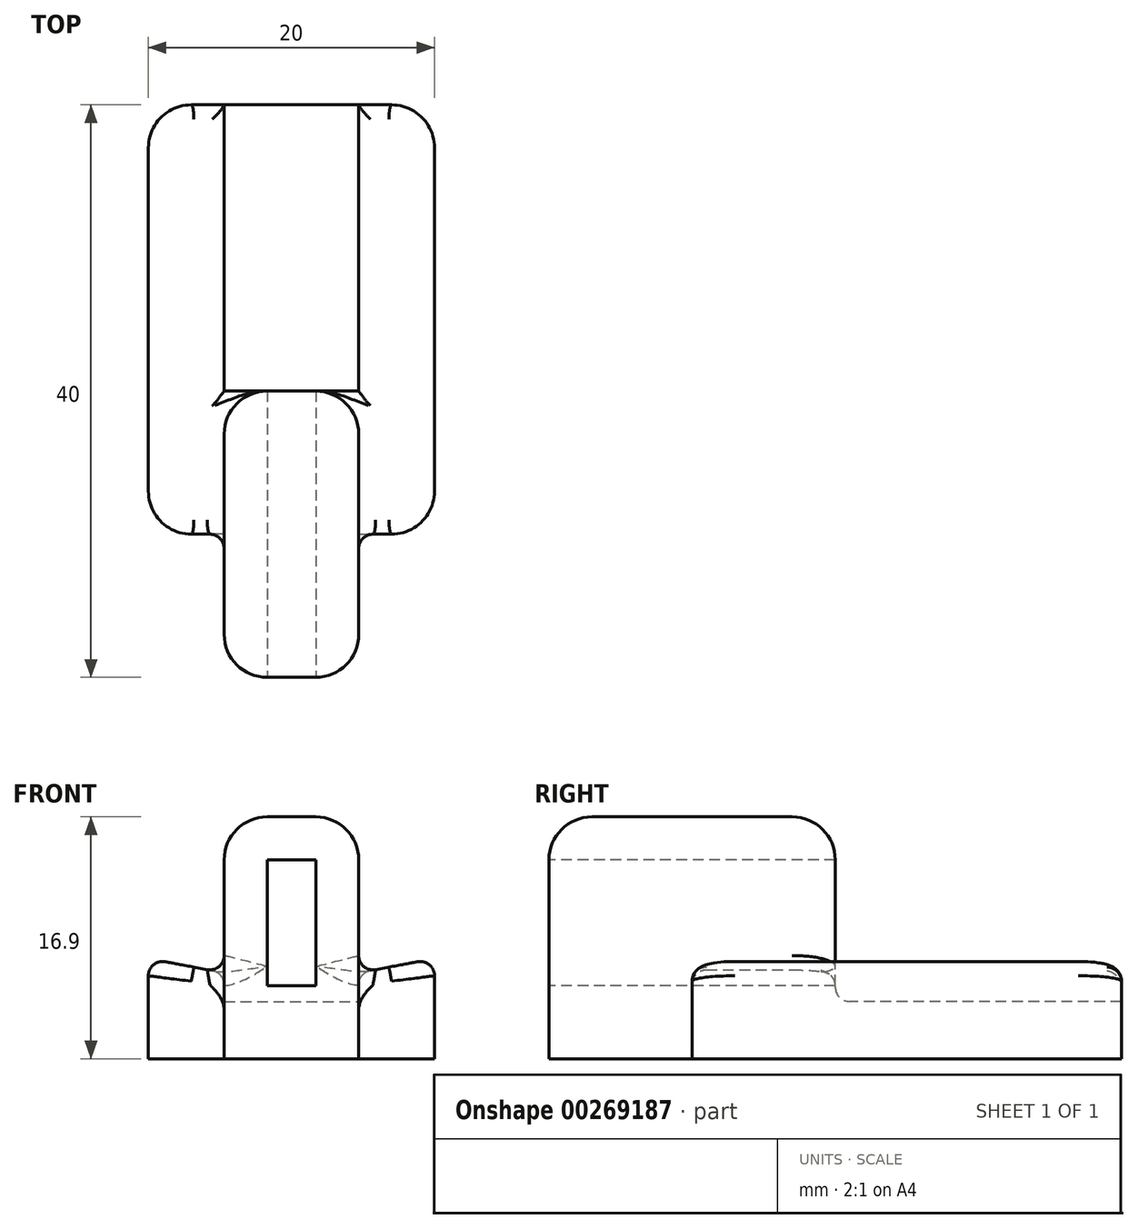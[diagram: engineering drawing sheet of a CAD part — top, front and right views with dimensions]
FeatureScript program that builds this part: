
annotation { "Feature Type Name" : "Feature", "Feature Type Description" : "" }
export const myFeature = defineFeature(function(context is Context, id is Id, definition is map)
    precondition{}
    {
        {
            assignVariable(context, id + "F0", {"name" : "BracketHeight", "anyValue" : 8.8});
        }
        {
            var Q0;
            Q0=qCreatedBy(makeId("Top.planeOp"),FACE);
            var sketch = newSketch(context, id + "F1", { "sketchPlane" : qUnion([Q0])});
            skLineSegment(sketch, "E0.bottom", {"start": v(4.7, -10) * mm, "end": v(-4.7, -10) * mm});
            skLineSegment(sketch, "E0.top", {"start": v(4.7, 10) * mm, "end": v(-4.7, 10) * mm});
            skLineSegment(sketch, "E0.left", {"start": v(4.7, -10) * mm, "end": v(4.7, 10) * mm});
            skLineSegment(sketch, "E0.right", {"start": v(-4.7, -10) * mm, "end": v(-4.7, 10) * mm});
            skPoint(sketch, "E0.middle", {"position": v(0, 0) * mm});
            skLineSegment(sketch, "E1", {"start": v(0, 23.9) * mm, "end": v(0, -29.95) * mm, "construction": true});
            skPoint(sketch, "E1.endSnap0", {"position": v(0, 10) * mm});
            skSolve(sketch);
        }
        {
            var Q0;
            Q0 = qSketchRegion(id + "F1", true);
            extrude(context, id + "F2", {"entities" : qUnion([Q0]), "depth" : (getVariable(context, 'BracketHeight') + 6) * mm});
        }
        {
            var Q0;
            Q0=makeQuery(id+"F2.opExtrude","SWEPT_FACE",FACE,{"disambiguationData":[OSD([sQuery(id+"F1.wireOp",EDGE,"E0.bottom")])]});
            var sketch = newSketch(context, id + "F3", { "sketchPlane" : qUnion([Q0])});
            skLineSegment(sketch, "E2.bottom", {"start": v(1.7, 11.8) * mm, "end": v(-1.7, 11.8) * mm});
            skLineSegment(sketch, "E2.top", {"start": v(1.7, 3) * mm, "end": v(-1.7, 3) * mm});
            skLineSegment(sketch, "E2.left", {"start": v(1.7, 11.8) * mm, "end": v(1.7, 3) * mm});
            skLineSegment(sketch, "E2.right", {"start": v(-1.7, 11.8) * mm, "end": v(-1.7, 3) * mm});
            skPoint(sketch, "E2.middle", {"position": v(0, 7.4) * mm});
            skLineSegment(sketch, "E3", {"start": v(-4.7, 14.8) * mm, "end": v(4.7, 0) * mm, "construction": true});
            skSolve(sketch);
        }
        {
            var Q0;
            Q0 = qSketchRegion(id + "F3", true);
            extrude(context, id + "F4", {"entities" : qUnion([Q0]), "operationType" : NewBodyOperationType.REMOVE, "endBound" : BoundingType.THROUGH_ALL, "oppositeDirection" : true, "depth" : 25 * mm});
        }
        {
            var Q0;
            Q0=qCreatedBy(makeId("Right.planeOp"),FACE);
            var sketch = newSketch(context, id + "F5", { "sketchPlane" : qUnion([Q0])});
            skLineSegment(sketch, "E4.bottom", {"start": v(0, 12.9) * mm, "end": v(30, 12.9) * mm});
            skLineSegment(sketch, "E4.top", {"start": v(0, 16.9) * mm, "end": v(30, 16.9) * mm});
            skLineSegment(sketch, "E4.left", {"start": v(0, 12.9) * mm, "end": v(0, 16.9) * mm});
            skLineSegment(sketch, "E4.right", {"start": v(30, 12.9) * mm, "end": v(30, 16.9) * mm});
            skSolve(sketch);
        }
        {
            var Q0;
            Q0 = qSketchRegion(id + "F5", true);
            extrude(context, id + "F6", {"entities" : qUnion([Q0]), "operationType" : NewBodyOperationType.ADD, "endBound" : BoundingType.SYMMETRIC, "depth" : 20 * mm, "hasSecondDirection" : true, "secondDirectionOppositeDirection" : true, "secondDirectionDepth" : 25 * mm});
        }
        {
            var Q0;
            Q0=makeQuery(id+"F2.opExtrude","CAP_FACE",FACE,{"disambiguationData":[OSD([sQuery(id+"F1.wireOp",EDGE,"E0.bottom"),sQuery(id+"F1.wireOp",EDGE,"E0.top"),sQuery(id+"F1.wireOp",EDGE,"E0.left"),sQuery(id+"F1.wireOp",EDGE,"E0.right")])],"isStart":false});
            var sketch = newSketch(context, id + "F7", { "sketchPlane" : qUnion([Q0])});
            skLineSegment(sketch, "E5.bottom", {"start": v(-4.7, 0) * mm, "end": v(4.7, 0) * mm});
            skLineSegment(sketch, "E5.top", {"start": v(-4.7, -10) * mm, "end": v(4.7, -10) * mm});
            skLineSegment(sketch, "E5.left", {"start": v(-4.7, 0) * mm, "end": v(-4.7, -10) * mm});
            skLineSegment(sketch, "E5.right", {"start": v(4.7, 0) * mm, "end": v(4.7, -10) * mm});
            skSolve(sketch);
        }
        {
            var Q0;
            Q0 = qSketchRegion(id + "F7", true);
            var Q1;
            Q1=makeQuery(id+"F6.opExtrude","SWEPT_FACE",FACE,{"disambiguationData":[OSD([sQuery(id+"F5.wireOp",EDGE,"E4.top")])]});
            extrude(context, id + "F8", {"entities" : qUnion([Q0]), "operationType" : NewBodyOperationType.ADD, "endBound" : BoundingType.UP_TO_SURFACE, "endBoundEntityFace" : qUnion([Q1]), "depth" : 25 * mm});
        }
        {
            var Q0;
            {var subQ1=sQuery(id+"F5.wireOp",EDGE,"E4.left");Q0=makeQuery(id+"F8.boolean.opBoolean","SPLIT",FACE,{"disambiguationData":[TD([makeQuery(id+"F2.opExtrude","SWEPT_FACE",FACE,{"disambiguationData":[OSD([sQuery(id+"F1.wireOp",EDGE,"E0.right")])]})])],"derivedFrom":makeQuery(id+"F6.opExtrude","SWEPT_FACE",FACE,{"disambiguationData":[OSD([subQ1])]})});}
            var sketch = newSketch(context, id + "F9", { "sketchPlane" : qUnion([Q0])});
            skLineSegment(sketch, "E6", {"start": v(-10, 12.9) * mm, "end": v(-10, 9.9) * mm});
            skLineSegment(sketch, "E7", {"start": v(-10, 9.9) * mm, "end": v(-4.7, 10.9) * mm});
            skLineSegment(sketch, "E8", {"start": v(-4.7, 10.9) * mm, "end": v(-4.7, 12.9) * mm});
            skLineSegment(sketch, "E9", {"start": v(-4.7, 12.9) * mm, "end": v(-10, 12.9) * mm});
            skLineSegment(sketch, "E10.MirrorCS", {"start": v(10, 9.9) * mm, "end": v(4.7, 10.9) * mm});
            skLineSegment(sketch, "E11.MirrorCS", {"start": v(10, 12.9) * mm, "end": v(10, 9.9) * mm});
            skLineSegment(sketch, "E12.MirrorCS", {"start": v(4.7, 10.9) * mm, "end": v(4.7, 12.9) * mm});
            skLineSegment(sketch, "E13.MirrorCS", {"start": v(4.7, 12.9) * mm, "end": v(10, 12.9) * mm});
            skSolve(sketch);
        }
        {
            var Q0;
            Q0 = qSketchRegion(id + "F9", true);
            var Q1;
            Q1=makeQuery(id+"F6.opExtrude","SWEPT_FACE",FACE,{"disambiguationData":[OSD([sQuery(id+"F5.wireOp",EDGE,"E4.right")])]});
            extrude(context, id + "F10", {"entities" : qUnion([Q0]), "operationType" : NewBodyOperationType.ADD, "endBound" : BoundingType.UP_TO_SURFACE, "oppositeDirection" : true, "endBoundEntityFace" : qUnion([Q1]), "depth" : 25 * mm});
        }
        {
            var Q0;
            Q0=makeQuery(id+"F2.opExtrude","SWEPT_BODY",BODY,{"disambiguationData":[OSD([sQuery(id+"F1.wireOp",EDGE,"E0.bottom"),sQuery(id+"F1.wireOp",EDGE,"E0.top"),sQuery(id+"F1.wireOp",EDGE,"E0.left"),sQuery(id+"F1.wireOp",EDGE,"E0.right")])]});
            var Q1;
            Q1=sQuery(id+"F1.wireOp",EDGE,"E1");
            transform(context, id + "F11", {"entities" : qUnion([Q0]), "transformType" : TransformType.ROTATION, "transformAxis" : qUnion([Q1]), "angle" : 180 * degree, "makeCopy" : false});
        }
        {
            var Q0;
            Q0=makeQuery(id+"F2.opExtrude","CAP_FACE",FACE,{"disambiguationData":[OSD([sQuery(id+"F1.wireOp",EDGE,"E0.bottom"),sQuery(id+"F1.wireOp",EDGE,"E0.top"),sQuery(id+"F1.wireOp",EDGE,"E0.left"),sQuery(id+"F1.wireOp",EDGE,"E0.right")])],"isStart":true});
            var Q1;
            Q1=makeQuery(id+"F8.boolean.opBoolean","MERGE",EDGE,{"derivedFrom":[makeQuery(id+"F2.opExtrude","SWEPT_EDGE",EDGE,{"disambiguationData":[OSD([sQuery(id+"F1.wireOp",EDGE,"E0.bottom"),sQuery(id+"F1.wireOp",EDGE,"E0.left")])]}),makeQuery(id+"F8.opExtrude","SWEPT_EDGE",EDGE,{"disambiguationData":[OSD([sQuery(id+"F7.wireOp",EDGE,"E5.top"),sQuery(id+"F7.wireOp",EDGE,"E5.right")])]})]});
            var Q2;
            Q2=makeQuery(id+"F8.boolean.opBoolean","MERGE",EDGE,{"derivedFrom":[makeQuery(id+"F2.opExtrude","SWEPT_EDGE",EDGE,{"disambiguationData":[OSD([sQuery(id+"F1.wireOp",EDGE,"E0.bottom"),sQuery(id+"F1.wireOp",EDGE,"E0.right")])]}),makeQuery(id+"F8.opExtrude","SWEPT_EDGE",EDGE,{"disambiguationData":[OSD([sQuery(id+"F7.wireOp",EDGE,"E5.top"),sQuery(id+"F7.wireOp",EDGE,"E5.left")])]})]});
            var Q3;
            {var subQ0=sQuery(id+"F1.wireOp",EDGE,"E0.left");var subQ1=sQuery(id+"F1.wireOp",EDGE,"E0.top");Q3=makeQuery(id+"F10.boolean.opBoolean","SPLIT",EDGE,{"disambiguationData":[TD([makeQuery(id+"F2.opExtrude","CAP_FACE",FACE,{"disambiguationData":[OSD([sQuery(id+"F1.wireOp",EDGE,"E0.bottom"),subQ1,subQ0,sQuery(id+"F1.wireOp",EDGE,"E0.right")])],"isStart":true})])],"derivedFrom":makeQuery(id+"F2.opExtrude","SWEPT_EDGE",EDGE,{"disambiguationData":[OSD([subQ1,subQ0])]})});}
            var Q4;
            {var subQ0=sQuery(id+"F1.wireOp",EDGE,"E0.right");var subQ1=sQuery(id+"F1.wireOp",EDGE,"E0.top");Q4=makeQuery(id+"F10.boolean.opBoolean","SPLIT",EDGE,{"disambiguationData":[TD([makeQuery(id+"F2.opExtrude","CAP_FACE",FACE,{"disambiguationData":[OSD([sQuery(id+"F1.wireOp",EDGE,"E0.bottom"),subQ1,sQuery(id+"F1.wireOp",EDGE,"E0.left"),subQ0])],"isStart":true})])],"derivedFrom":makeQuery(id+"F2.opExtrude","SWEPT_EDGE",EDGE,{"disambiguationData":[OSD([subQ1,subQ0])]})});}
            var Q5;
            Q5=makeQuery(id+"F10.boolean.opBoolean","MERGE",EDGE,{"derivedFrom":[makeQuery(id+"F6.opExtrude","CAP_EDGE",EDGE,{"disambiguationData":[OSD([sQuery(id+"F5.wireOp",EDGE,"E4.left")])],"isStart":false}),makeQuery(id+"F10.opExtrude","CAP_EDGE",EDGE,{"disambiguationData":[OSD([sQuery(id+"F9.wireOp",EDGE,"E11.MirrorCS")])],"isStart":true})]});
            var Q6;
            Q6=makeQuery(id+"F10.boolean.opBoolean","MERGE",EDGE,{"derivedFrom":[makeQuery(id+"F6.opExtrude","CAP_EDGE",EDGE,{"disambiguationData":[OSD([sQuery(id+"F5.wireOp",EDGE,"E4.left")])],"isStart":true}),makeQuery(id+"F10.opExtrude","CAP_EDGE",EDGE,{"disambiguationData":[OSD([sQuery(id+"F9.wireOp",EDGE,"E6")])],"isStart":true})]});
            var Q7;
            {var subQ0=sQuery(id+"F5.wireOp",EDGE,"E4.right");Q7=makeQuery(id+"F10.boolean.opBoolean","MERGE",EDGE,{"derivedFrom":[makeQuery(id+"F6.opExtrude","CAP_EDGE",EDGE,{"disambiguationData":[OSD([subQ0])],"isStart":true}),makeQuery(id+"F10.opExtrude","TWEAK_EDGE",EDGE,{"derivedFrom":[makeQuery(id+"F6.opExtrude","SWEPT_FACE",FACE,{"disambiguationData":[OSD([subQ0])]}),makeQuery(id+"F9.imprint","IMPRINT",EDGE,{"derivedFrom":sQuery(id+"F9.wireOp",EDGE,"E6")})]})]});}
            var Q8;
            {var subQ0=sQuery(id+"F5.wireOp",EDGE,"E4.right");Q8=makeQuery(id+"F10.boolean.opBoolean","MERGE",EDGE,{"derivedFrom":[makeQuery(id+"F6.opExtrude","CAP_EDGE",EDGE,{"disambiguationData":[OSD([subQ0])],"isStart":false}),makeQuery(id+"F10.opExtrude","TWEAK_EDGE",EDGE,{"derivedFrom":[makeQuery(id+"F6.opExtrude","SWEPT_FACE",FACE,{"disambiguationData":[OSD([subQ0])]}),makeQuery(id+"F9.imprint","IMPRINT",EDGE,{"derivedFrom":sQuery(id+"F9.wireOp",EDGE,"E11.MirrorCS")})]})]});}
            fillet(context, id + "F12", {"entities" : qUnion([Q0, Q1, Q2, Q3, Q4, Q5, Q6, Q7, Q8]), "radius" : 3 * mm, "tangentPropagation" : true, "allowEdgeOverflow" : false});
        }
        {
            var Q0;
            {var subQ0=makeQuery(id+"F10.opExtrude","SWEPT_FACE",FACE,{"disambiguationData":[OSD([sQuery(id+"F9.wireOp",EDGE,"E10.MirrorCS")])]});var subQ1=sQuery(id+"F1.wireOp",EDGE,"E0.left");var subQ2=sQuery(id+"F1.wireOp",EDGE,"E0.top");Q0=makeQuery(id+"F12.opFillet","BLEND_EDGE",EDGE,{"blendedFrom":[makeQuery(id+"F10.boolean.opBoolean","SPLIT",EDGE,{"disambiguationData":[TD([makeQuery(id+"F2.opExtrude","CAP_FACE",FACE,{"disambiguationData":[OSD([sQuery(id+"F1.wireOp",EDGE,"E0.bottom"),subQ2,subQ1,sQuery(id+"F1.wireOp",EDGE,"E0.right")])],"isStart":true})])],"derivedFrom":makeQuery(id+"F2.opExtrude","SWEPT_EDGE",EDGE,{"disambiguationData":[OSD([subQ2,subQ1])]})}),subQ0],"blendedInto":[subQ0]});}
            var Q1;
            {var subQ0=makeQuery(id+"F10.opExtrude","SWEPT_FACE",FACE,{"disambiguationData":[OSD([sQuery(id+"F9.wireOp",EDGE,"E7")])]});var subQ1=sQuery(id+"F1.wireOp",EDGE,"E0.right");var subQ2=sQuery(id+"F1.wireOp",EDGE,"E0.top");Q1=makeQuery(id+"F12.opFillet","BLEND_EDGE",EDGE,{"blendedFrom":[makeQuery(id+"F10.boolean.opBoolean","SPLIT",EDGE,{"disambiguationData":[TD([makeQuery(id+"F2.opExtrude","CAP_FACE",FACE,{"disambiguationData":[OSD([sQuery(id+"F1.wireOp",EDGE,"E0.bottom"),subQ2,sQuery(id+"F1.wireOp",EDGE,"E0.left"),subQ1])],"isStart":true})])],"derivedFrom":makeQuery(id+"F2.opExtrude","SWEPT_EDGE",EDGE,{"disambiguationData":[OSD([subQ2,subQ1])]})}),subQ0],"blendedInto":[subQ0]});}
            var Q2;
            Q2=makeQuery(id+"F10.opExtrude","SWEPT_EDGE",EDGE,{"disambiguationData":[OSD([sQuery(id+"F9.wireOp",EDGE,"E12.MirrorCS"),sQuery(id+"F9.wireOp",EDGE,"E13.MirrorCS")])]});
            var Q3;
            Q3=makeQuery(id+"F10.opExtrude","SWEPT_EDGE",EDGE,{"disambiguationData":[OSD([sQuery(id+"F1.wireOp",EDGE,"E0.right"),sQuery(id+"F5.wireOp",EDGE,"E4.left"),sQuery(id+"F7.wireOp",EDGE,"E5.bottom"),sQuery(id+"F7.wireOp",EDGE,"E5.left"),sQuery(id+"F9.wireOp",EDGE,"E8"),sQuery(id+"F9.wireOp",EDGE,"E9")])]});
            var Q4;
            Q4=makeQuery(id+"F6.boolean.opBoolean","INTERSECT",EDGE,{"derivedFrom":[makeQuery(id+"F2.opExtrude","SWEPT_FACE",FACE,{"disambiguationData":[OSD([sQuery(id+"F1.wireOp",EDGE,"E0.top")])]}),makeQuery(id+"F6.opExtrude","SWEPT_FACE",FACE,{"disambiguationData":[OSD([sQuery(id+"F5.wireOp",EDGE,"E4.bottom")])]})]});
            var Q5;
            Q5=makeQuery(id+"F10.opExtrude","TWEAK_EDGE",EDGE,{"derivedFrom":[makeQuery(id+"F6.opExtrude","SWEPT_FACE",FACE,{"disambiguationData":[OSD([sQuery(id+"F5.wireOp",EDGE,"E4.right")])]}),makeQuery(id+"F9.imprint","IMPRINT",EDGE,{"derivedFrom":sQuery(id+"F9.wireOp",EDGE,"E12.MirrorCS")})]});
            var Q6;
            Q6=makeQuery(id+"F10.opExtrude","TWEAK_EDGE",EDGE,{"derivedFrom":[makeQuery(id+"F6.opExtrude","SWEPT_FACE",FACE,{"disambiguationData":[OSD([sQuery(id+"F5.wireOp",EDGE,"E4.right")])]}),makeQuery(id+"F9.imprint","IMPRINT",EDGE,{"derivedFrom":sQuery(id+"F9.wireOp",EDGE,"E10.MirrorCS")})]});
            var Q7;
            Q7=makeQuery(id+"F10.opExtrude","TWEAK_EDGE",EDGE,{"derivedFrom":[makeQuery(id+"F6.opExtrude","SWEPT_FACE",FACE,{"disambiguationData":[OSD([sQuery(id+"F5.wireOp",EDGE,"E4.right")])]}),makeQuery(id+"F9.imprint","IMPRINT",EDGE,{"derivedFrom":sQuery(id+"F9.wireOp",EDGE,"E7")})]});
            var Q8;
            Q8=makeQuery(id+"F10.opExtrude","SWEPT_EDGE",EDGE,{"disambiguationData":[OSD([sQuery(id+"F9.wireOp",EDGE,"E10.MirrorCS"),sQuery(id+"F9.wireOp",EDGE,"E11.MirrorCS")])]});
            var Q9;
            Q9=makeQuery(id+"F10.opExtrude","SWEPT_EDGE",EDGE,{"disambiguationData":[OSD([sQuery(id+"F9.wireOp",EDGE,"E6"),sQuery(id+"F9.wireOp",EDGE,"E7")])]});
            var Q10;
            Q10=makeQuery(id+"F10.opExtrude","CAP_EDGE",EDGE,{"disambiguationData":[OSD([sQuery(id+"F9.wireOp",EDGE,"E7")])],"isStart":true});
            var Q11;
            Q11=makeQuery(id+"F10.opExtrude","CAP_EDGE",EDGE,{"disambiguationData":[OSD([sQuery(id+"F9.wireOp",EDGE,"E10.MirrorCS")])],"isStart":true});
            var Q12;
            {var subQ0=sQuery(id+"F5.wireOp",EDGE,"E4.right");var subQ1=sQuery(id+"F9.wireOp",EDGE,"E8");var subQ2=sQuery(id+"F9.wireOp",EDGE,"E7");Q12=makeQuery(id+"F10.boolean.opBoolean","SPLIT",EDGE,{"disambiguationData":[TD([makeQuery(id+"F6.opExtrude","SWEPT_FACE",FACE,{"disambiguationData":[OSD([subQ0])]})])],"derivedFrom":makeQuery(id+"F10.opExtrude","SWEPT_EDGE",EDGE,{"disambiguationData":[OSD([subQ2,subQ1])]})});}
            var Q13;
            {var subQ0=sQuery(id+"F5.wireOp",EDGE,"E4.right");var subQ1=sQuery(id+"F9.wireOp",EDGE,"E12.MirrorCS");var subQ2=sQuery(id+"F9.wireOp",EDGE,"E10.MirrorCS");Q13=makeQuery(id+"F10.boolean.opBoolean","SPLIT",EDGE,{"disambiguationData":[TD([makeQuery(id+"F6.opExtrude","SWEPT_FACE",FACE,{"disambiguationData":[OSD([subQ0])]})])],"derivedFrom":makeQuery(id+"F10.opExtrude","SWEPT_EDGE",EDGE,{"disambiguationData":[OSD([subQ2,subQ1])]})});}
            fillet(context, id + "F13", {"entities" : qUnion([Q0, Q1, Q2, Q3, Q4, Q5, Q6, Q7, Q8, Q9, Q10, Q11, Q12, Q13]), "radius" : 1 * mm, "tangentPropagation" : true, "allowEdgeOverflow" : false});
        }
        {
            var Q0;
            {var subQ0=sQuery(id+"F1.wireOp",EDGE,"E0.top");var subQ1=makeQuery(id+"F2.opExtrude","SWEPT_FACE",FACE,{"disambiguationData":[OSD([subQ0])]});var subQ2=makeQuery(id+"F10.opExtrude","SWEPT_FACE",FACE,{"disambiguationData":[OSD([sQuery(id+"F9.wireOp",EDGE,"E7")])]});var subQ3=sQuery(id+"F1.wireOp",EDGE,"E0.right");Q0=makeQuery(id+"F13.opFillet","BLEND_EDGE",EDGE,{"blendedFrom":[makeQuery(id+"F12.opFillet","BLEND_EDGE",EDGE,{"blendedFrom":[makeQuery(id+"F10.boolean.opBoolean","SPLIT",EDGE,{"disambiguationData":[TD([makeQuery(id+"F2.opExtrude","CAP_FACE",FACE,{"disambiguationData":[OSD([sQuery(id+"F1.wireOp",EDGE,"E0.bottom"),subQ0,sQuery(id+"F1.wireOp",EDGE,"E0.left"),subQ3])],"isStart":true})])],"derivedFrom":makeQuery(id+"F2.opExtrude","SWEPT_EDGE",EDGE,{"disambiguationData":[OSD([subQ0,subQ3])]})}),subQ2],"blendedInto":[subQ2]}),subQ1],"blendedInto":[subQ1]});}
            var Q1;
            {var subQ0=sQuery(id+"F1.wireOp",EDGE,"E0.top");var subQ1=makeQuery(id+"F2.opExtrude","SWEPT_FACE",FACE,{"disambiguationData":[OSD([subQ0])]});var subQ2=makeQuery(id+"F10.opExtrude","SWEPT_FACE",FACE,{"disambiguationData":[OSD([sQuery(id+"F9.wireOp",EDGE,"E10.MirrorCS")])]});var subQ3=sQuery(id+"F1.wireOp",EDGE,"E0.left");Q1=makeQuery(id+"F13.opFillet","BLEND_EDGE",EDGE,{"blendedFrom":[makeQuery(id+"F12.opFillet","BLEND_EDGE",EDGE,{"blendedFrom":[makeQuery(id+"F10.boolean.opBoolean","SPLIT",EDGE,{"disambiguationData":[TD([makeQuery(id+"F2.opExtrude","CAP_FACE",FACE,{"disambiguationData":[OSD([sQuery(id+"F1.wireOp",EDGE,"E0.bottom"),subQ0,subQ3,sQuery(id+"F1.wireOp",EDGE,"E0.right")])],"isStart":true})])],"derivedFrom":makeQuery(id+"F2.opExtrude","SWEPT_EDGE",EDGE,{"disambiguationData":[OSD([subQ0,subQ3])]})}),subQ2],"blendedInto":[subQ2]}),subQ1],"blendedInto":[subQ1]});}
            fillet(context, id + "F14", {"entities" : qUnion([Q0, Q1]), "radius" : 1 * mm, "tangentPropagation" : true, "allowEdgeOverflow" : false});
        }
    });
